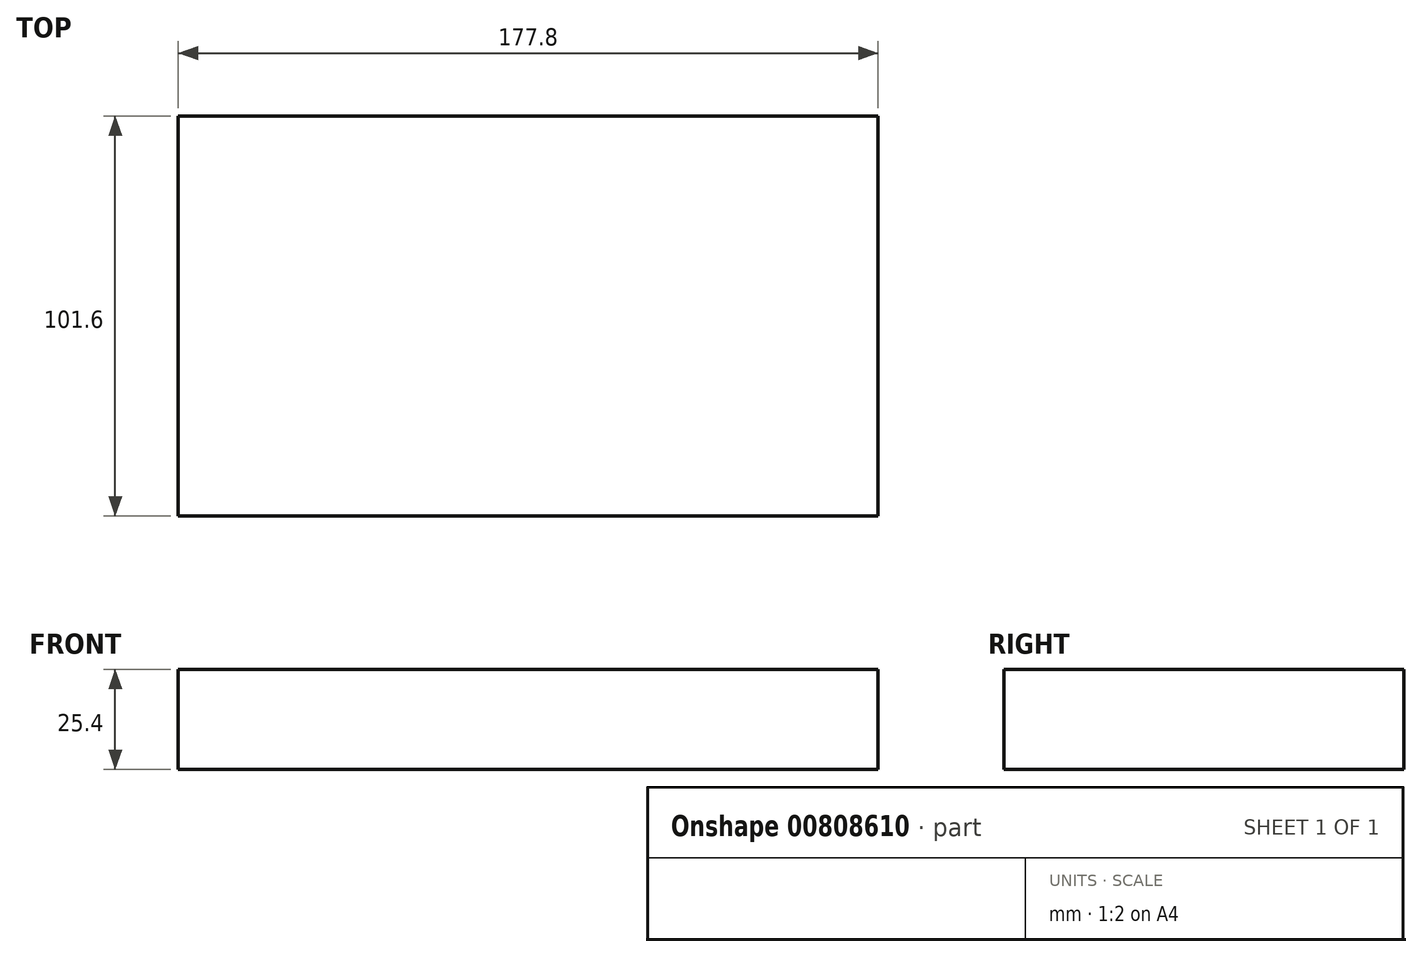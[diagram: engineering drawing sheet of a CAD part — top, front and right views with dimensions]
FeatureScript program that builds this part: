
annotation { "Feature Type Name" : "Feature", "Feature Type Description" : "" }
export const myFeature = defineFeature(function(context is Context, id is Id, definition is map)
    precondition{}
    {
        {
            var Q0;
            Q0=qCreatedBy(makeId("Top.planeOp"),FACE);
            var sketch = newSketch(context, id + "F0", { "sketchPlane" : qUnion([Q0])});
            skLineSegment(sketch, "E0.bottom", {"start": v(156.32, 0) * mm, "end": v(-21.48, 0) * mm});
            skLineSegment(sketch, "E0.top", {"start": v(156.32, 101.6) * mm, "end": v(-21.48, 101.6) * mm});
            skLineSegment(sketch, "E0.left", {"start": v(156.32, 0) * mm, "end": v(156.32, 101.6) * mm});
            skLineSegment(sketch, "E0.right", {"start": v(-21.48, 0) * mm, "end": v(-21.48, 101.6) * mm});
            skSolve(sketch);
        }
        {
            var Q0;
            Q0=makeQuery(id+"F0.imprint","IMPRINT",FACE,{"disambiguationData":[TD([[makeQuery(id+"F0.imprint","IMPRINT",EDGE,{"derivedFrom":sQuery(id+"F0.wireOp",EDGE,"E0.bottom")}),-1.0]])]});
            extrude(context, id + "F1", {"entities" : qUnion([Q0]), "depth" : 25.4 * mm, "offsetDistance" : 25.4 * mm});
        }
    });
